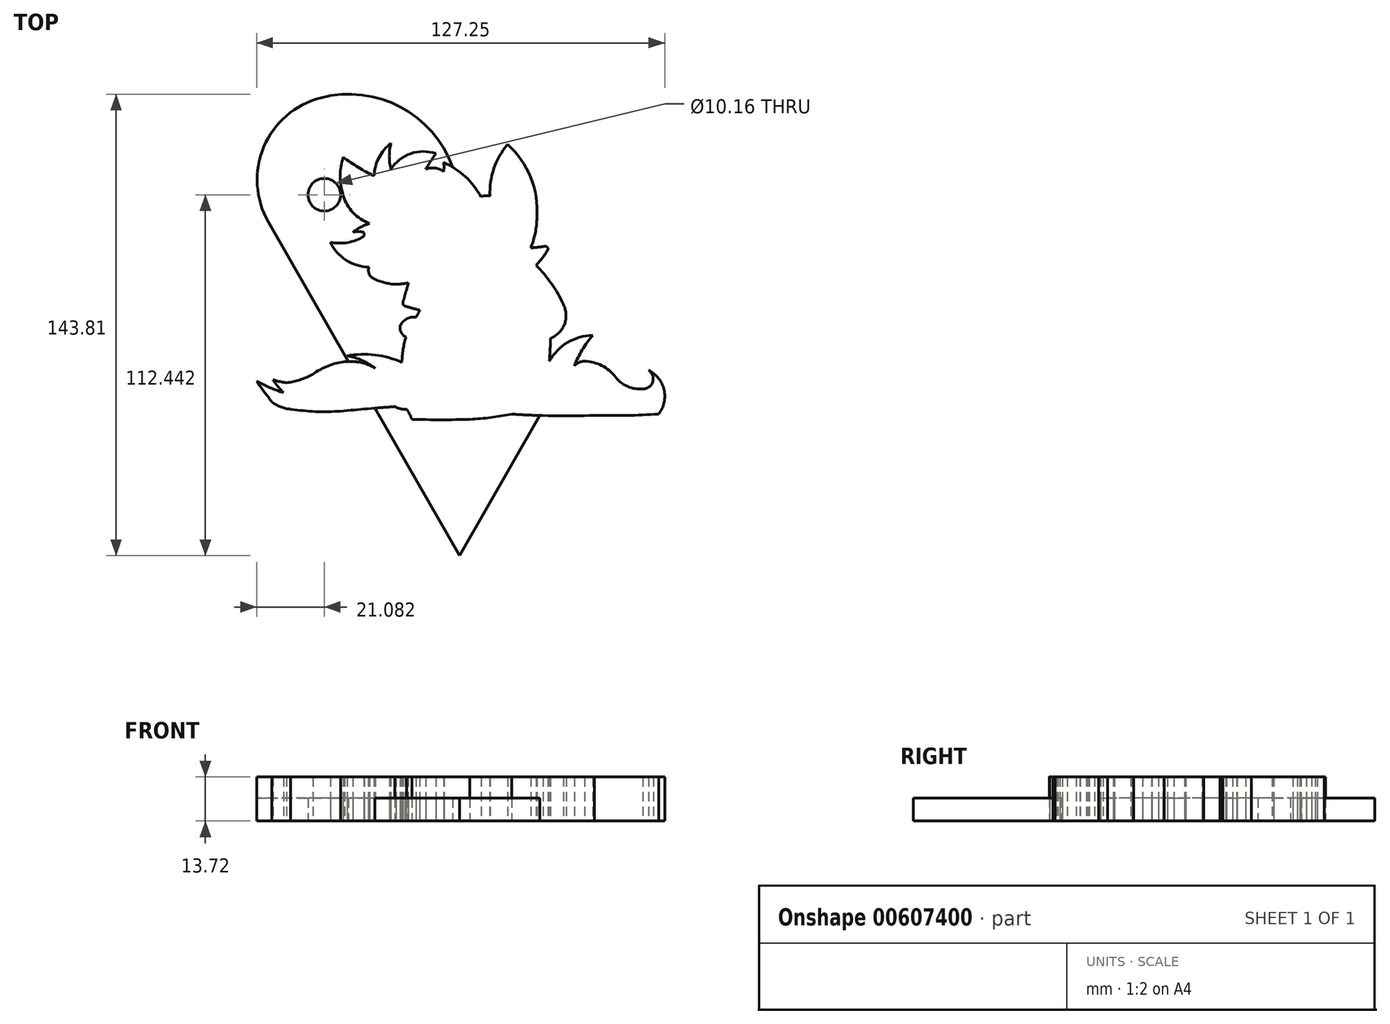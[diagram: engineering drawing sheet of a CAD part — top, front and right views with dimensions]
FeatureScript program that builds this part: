
annotation { "Feature Type Name" : "Feature", "Feature Type Description" : "" }
export const myFeature = defineFeature(function(context is Context, id is Id, definition is map)
    precondition{}
    {
        {
            var Q0;
            Q0=qCreatedBy(makeId("Top.planeOp"),FACE);
            var sketch = newSketch(context, id + "F0", { "sketchPlane" : qUnion([Q0])});
            skArc(sketch, "E0", {"start": v(-40.37, 7.34) * mm, "mid": v(-35.43, 1.75) * mm, "end": v(-28.28, -0.4) * mm});
            skArc(sketch, "E1", {"start": v(-28.28, -0.4) * mm, "mid": v(-28.3, -2.46) * mm, "end": v(-26.9, -3.99) * mm});
            skArc(sketch, "E2", {"start": v(-26.9, -3.99) * mm, "mid": v(-23.5, -5.25) * mm, "end": v(-19.91, -5.8) * mm});
            skArc(sketch, "E3", {"start": v(-19.91, -5.8) * mm, "mid": v(-17.97, -5.63) * mm, "end": v(-16.04, -5.38) * mm});
            skArc(sketch, "E4", {"start": v(-17.13, -9.12) * mm, "mid": v(-16.52, -7.27) * mm, "end": v(-16.04, -5.38) * mm});
            skArc(sketch, "E5", {"start": v(-17.65, -11.1) * mm, "mid": v(-17.34, -10.13) * mm, "end": v(-17.13, -9.12) * mm});
            skArc(sketch, "E6", {"start": v(-17.65, -11.1) * mm, "mid": v(-17.7, -11.94) * mm, "end": v(-17.13, -12.56) * mm});
            skArc(sketch, "E7", {"start": v(-17.13, -12.56) * mm, "mid": v(-14.8, -13.21) * mm, "end": v(-12.46, -13.87) * mm});
            skArc(sketch, "E8", {"start": v(-12.46, -13.87) * mm, "mid": v(-13.05, -14.97) * mm, "end": v(-13.6, -16.08) * mm});
            skArc(sketch, "E9", {"start": v(-13.6, -16.08) * mm, "mid": v(-16.6, -16.57) * mm, "end": v(-18.61, -18.86) * mm});
            skArc(sketch, "E10", {"start": v(-18.61, -18.86) * mm, "mid": v(-18.28, -20.87) * mm, "end": v(-16.75, -22.22) * mm});
            skArc(sketch, "E11", {"start": v(-16.75, -22.22) * mm, "mid": v(-17.7, -26.1) * mm, "end": v(-18.04, -30.06) * mm});
            skArc(sketch, "E12", {"start": v(-18.04, -30.06) * mm, "mid": v(-26.4, -27.8) * mm, "end": v(-35.06, -28.06) * mm});
            skArc(sketch, "E13", {"start": v(-26.36, -31.93) * mm, "mid": v(-30.48, -29.47) * mm, "end": v(-35.06, -28.06) * mm});
            skArc(sketch, "E14", {"start": v(-26.36, -31.93) * mm, "mid": v(-30.95, -30.12) * mm, "end": v(-35.86, -29.92) * mm});
            skArc(sketch, "E15", {"start": v(-35.86, -29.92) * mm, "mid": v(-41.1, -31.2) * mm, "end": v(-45.82, -33.82) * mm});
            skArc(sketch, "E16", {"start": v(-54.02, -36.45) * mm, "mid": v(-49.8, -35.53) * mm, "end": v(-45.82, -33.82) * mm});
            skArc(sketch, "E17", {"start": v(-58.23, -35.53) * mm, "mid": v(-56.14, -36.1) * mm, "end": v(-54.02, -36.45) * mm});
            skArc(sketch, "E18", {"start": v(-58.23, -35.53) * mm, "mid": v(-56.69, -37.64) * mm, "end": v(-54.93, -39.57) * mm});
            skArc(sketch, "E19", {"start": v(-63.33, -35.96) * mm, "mid": v(-59.21, -37.96) * mm, "end": v(-54.93, -39.57) * mm});
            skArc(sketch, "E20", {"start": v(-63.33, -35.96) * mm, "mid": v(-61.02, -39.24) * mm, "end": v(-58.55, -42.4) * mm});
            skArc(sketch, "E21", {"start": v(-58.55, -42.4) * mm, "mid": v(-55.81, -44.01) * mm, "end": v(-52.7, -44.68) * mm});
            skArc(sketch, "E22", {"start": v(-52.7, -44.68) * mm, "mid": v(-44.95, -45.44) * mm, "end": v(-37.16, -45.3) * mm});
            skArc(sketch, "E23", {"start": v(-20.24, -43.88) * mm, "mid": v(-28.7, -44.56) * mm, "end": v(-37.16, -45.3) * mm});
            skArc(sketch, "E24", {"start": v(-20.24, -43.88) * mm, "mid": v(-18.46, -44.58) * mm, "end": v(-16.55, -44.68) * mm});
            skArc(sketch, "E25", {"start": v(-14.9, -47.86) * mm, "mid": v(-15.65, -46.23) * mm, "end": v(-16.55, -44.68) * mm});
            skArc(sketch, "E26", {"start": v(-14.9, -47.86) * mm, "mid": v(-5.87, -48) * mm, "end": v(3.17, -47.86) * mm});
            skArc(sketch, "E27", {"start": v(3.17, -47.86) * mm, "mid": v(9.74, -47.27) * mm, "end": v(16.25, -46.21) * mm});
            skArc(sketch, "E28", {"start": v(16.25, -46.21) * mm, "mid": v(29.1, -46.76) * mm, "end": v(41.96, -46.59) * mm});
            skArc(sketch, "E29", {"start": v(41.96, -46.59) * mm, "mid": v(52, -46.65) * mm, "end": v(62.02, -46.21) * mm});
            skArc(sketch, "E30", {"start": v(62.02, -46.21) * mm, "mid": v(63.69, -38.64) * mm, "end": v(58.88, -32.56) * mm});
            skArc(sketch, "E31", {"start": v(57.1, -38.36) * mm, "mid": v(60.2, -36.14) * mm, "end": v(58.88, -32.56) * mm});
            skArc(sketch, "E32", {"start": v(48.61, -34.71) * mm, "mid": v(52.37, -37.65) * mm, "end": v(57.1, -38.36) * mm});
            skArc(sketch, "E33", {"start": v(48.61, -34.71) * mm, "mid": v(44.3, -31.11) * mm, "end": v(38.87, -29.74) * mm});
            skArc(sketch, "E34", {"start": v(38.87, -29.74) * mm, "mid": v(37.14, -30.14) * mm, "end": v(35.72, -31.21) * mm});
            skArc(sketch, "E35", {"start": v(41.46, -21.68) * mm, "mid": v(38.2, -26.21) * mm, "end": v(35.72, -31.21) * mm});
            skArc(sketch, "E36", {"start": v(41.46, -21.68) * mm, "mid": v(33.63, -23.91) * mm, "end": v(27.94, -29.74) * mm});
            skArc(sketch, "E37", {"start": v(27.94, -29.74) * mm, "mid": v(28.17, -26.17) * mm, "end": v(28.29, -22.6) * mm});
            skArc(sketch, "E38", {"start": v(28.29, -22.6) * mm, "mid": v(32.65, -18.26) * mm, "end": v(32.34, -12.11) * mm});
            skArc(sketch, "E39", {"start": v(32.34, -12.11) * mm, "mid": v(28.62, -5.58) * mm, "end": v(23.77, 0.16) * mm});
            skArc(sketch, "E40", {"start": v(23.77, 0.16) * mm, "mid": v(25.84, 2.55) * mm, "end": v(27.56, 5.2) * mm});
            skArc(sketch, "E41", {"start": v(27.56, 5.2) * mm, "mid": v(26.99, 6) * mm, "end": v(26, 5.94) * mm});
            skArc(sketch, "E42", {"start": v(26, 5.94) * mm, "mid": v(24.06, 5.75) * mm, "end": v(22.12, 5.53) * mm});
            skArc(sketch, "E43", {"start": v(22.12, 5.53) * mm, "mid": v(23.52, 10.17) * mm, "end": v(24.03, 14.99) * mm});
            skArc(sketch, "E44", {"start": v(24.03, 14.99) * mm, "mid": v(22.16, 27.47) * mm, "end": v(14.92, 37.8) * mm});
            skArc(sketch, "E45", {"start": v(9.41, 21.73) * mm, "mid": v(7.98, 21.87) * mm, "end": v(6.6, 21.45) * mm});
            skArc(sketch, "E46", {"start": v(14.92, 37.8) * mm, "mid": v(10.64, 30.29) * mm, "end": v(9.41, 21.73) * mm});
            skArc(sketch, "E47", {"start": v(6.6, 21.45) * mm, "mid": v(1.7, 27.8) * mm, "end": v(-5.02, 32.18) * mm});
            skArc(sketch, "E48", {"start": v(-5.02, 29.37) * mm, "mid": v(-4.92, 30.77) * mm, "end": v(-5.02, 32.18) * mm});
            skArc(sketch, "E49", {"start": v(-5.02, 29.37) * mm, "mid": v(-7.72, 30.46) * mm, "end": v(-10.6, 30.08) * mm});
            skArc(sketch, "E50", {"start": v(-7.42, 34.97) * mm, "mid": v(-9.08, 32.57) * mm, "end": v(-10.6, 30.08) * mm});
            skArc(sketch, "E51", {"start": v(-7.42, 34.97) * mm, "mid": v(-15.29, 34.96) * mm, "end": v(-21.46, 30.08) * mm});
            skArc(sketch, "E52", {"start": v(-21.46, 38.17) * mm, "mid": v(-21.97, 34.12) * mm, "end": v(-21.46, 30.08) * mm});
            skArc(sketch, "E53", {"start": v(-21.46, 38.17) * mm, "mid": v(-25.21, 33.69) * mm, "end": v(-26.7, 28.04) * mm});
            skArc(sketch, "E54", {"start": v(-36.33, 33.86) * mm, "mid": v(-31.67, 30.69) * mm, "end": v(-26.7, 28.04) * mm});
            skArc(sketch, "E55", {"start": v(-40.37, 7.34) * mm, "mid": v(-34.96, 7.25) * mm, "end": v(-29.9, 9.18) * mm});
            skArc(sketch, "E56", {"start": v(-29.9, 9.18) * mm, "mid": v(-29.82, 9.8) * mm, "end": v(-29.9, 10.43) * mm});
            skArc(sketch, "E57", {"start": v(-29.9, 10.43) * mm, "mid": v(-31.64, 10.64) * mm, "end": v(-33.37, 10.43) * mm});
            skArc(sketch, "E58", {"start": v(-28.1, 13.2) * mm, "mid": v(-30.86, 12.05) * mm, "end": v(-33.37, 10.43) * mm});
            skArc(sketch, "E59", {"start": v(-36.33, 21.97) * mm, "mid": v(-33.3, 16.58) * mm, "end": v(-28.1, 13.2) * mm});
            skArc(sketch, "E60", {"start": v(-36.33, 33.86) * mm, "mid": v(-37.3, 27.91) * mm, "end": v(-36.33, 21.97) * mm});
            skSolve(sketch);
        }
        {
            var Q0;
            Q0=makeQuery(id+"F0.imprint","IMPRINT",FACE,{"disambiguationData":[TD([[makeQuery(id+"F0.imprint","IMPRINT",EDGE,{"derivedFrom":sQuery(id+"F0.wireOp",EDGE,"E0")}),1.0]])]});
            var sketch = newSketch(context, id + "F1", { "sketchPlane" : qUnion([Q0])});
            skLineSegment(sketch, "E61", {"start": v(-59.66, 13.61) * mm, "end": v(-0.11, -90.32) * mm});
            skArc(sketch, "E62", {"start": v(-43.38, 52.36) * mm, "mid": v(-61.1, 37) * mm, "end": v(-59.66, 13.61) * mm});
            skArc(sketch, "E63", {"start": v(-0.11, 18.97) * mm, "mid": v(-13.54, 46.3) * mm, "end": v(-43.38, 52.36) * mm});
            skArc(sketch, "E64.MirrorCS", {"start": v(-0.11, 18.97) * mm, "mid": v(13.32, 46.3) * mm, "end": v(43.16, 52.36) * mm});
            skLineSegment(sketch, "E65.MirrorCS", {"start": v(59.44, 13.61) * mm, "end": v(-0.11, -90.32) * mm});
            skArc(sketch, "E66.MirrorCS", {"start": v(43.16, 52.36) * mm, "mid": v(60.88, 37) * mm, "end": v(59.44, 13.61) * mm});
            skSolve(sketch);
        }
        {
            var Q0;
            {var subQ5=sQuery(id+"F1.wireOp",EDGE,"E62");Q0=makeQuery(id+"F1.imprint","IMPRINT",FACE,{"disambiguationData":[TD([[makeQuery(id+"F1.imprint","IMPRINT",EDGE,{"derivedFrom":subQ5}),1.0]])]});}
            var Q1;
            {var subQ0=sQuery(id+"F1.wireOp",EDGE,"E66.MirrorCS");Q1=makeQuery(id+"F1.imprint","IMPRINT",FACE,{"disambiguationData":[TD([[makeQuery(id+"F1.imprint","IMPRINT",EDGE,{"derivedFrom":subQ0}),-1.0]])]});}
            var Q2;
            {var subQ0=makeQuery(id+"F0.imprint","IMPRINT",EDGE,{"derivedFrom":sQuery(id+"F0.wireOp",EDGE,"E24")});Q2=makeQuery(id+"F1.imprint","IMPRINT",FACE,{"disambiguationData":[TD([[makeQuery(id+"F1.imprint","IMPRINT",EDGE,{"derivedFrom":subQ0}),-1.0]])]});}
            extrude(context, id + "F2", {"entities" : qUnion([Q0, Q1, Q2]), "depth" : 7.11 * mm, "offsetDistance" : 25.4 * mm});
        }
        {
            var Q0;
            Q0=makeQuery(id+"F0.imprint","IMPRINT",FACE,{"disambiguationData":[TD([[makeQuery(id+"F0.imprint","IMPRINT",EDGE,{"derivedFrom":sQuery(id+"F0.wireOp",EDGE,"E0")}),1.0]])]});
            extrude(context, id + "F3", {"entities" : qUnion([Q0]), "depth" : 13.72 * mm, "offsetDistance" : 25.4 * mm});
        }
        {
            var Q0;
            Q0=sQuery(id+"F0.wireOp",VERTEX,"E22.center");
            var Q1;
            Q1=makeQuery(id+"F2.opExtrude","SWEPT_BODY",BODY,{"disambiguationData":[OSD([sQuery(id+"F0.wireOp",EDGE,"E0"),sQuery(id+"F0.wireOp",EDGE,"E1"),sQuery(id+"F0.wireOp",EDGE,"E2"),sQuery(id+"F0.wireOp",EDGE,"E3"),sQuery(id+"F0.wireOp",EDGE,"E4"),sQuery(id+"F0.wireOp",EDGE,"E5"),sQuery(id+"F0.wireOp",EDGE,"E6"),sQuery(id+"F0.wireOp",EDGE,"E7"),sQuery(id+"F0.wireOp",EDGE,"E8"),sQuery(id+"F0.wireOp",EDGE,"E9"),sQuery(id+"F0.wireOp",EDGE,"E10"),sQuery(id+"F0.wireOp",EDGE,"E11"),sQuery(id+"F0.wireOp",EDGE,"E12"),sQuery(id+"F0.wireOp",EDGE,"E13"),sQuery(id+"F0.wireOp",EDGE,"E14"),sQuery(id+"F0.wireOp",EDGE,"E47"),sQuery(id+"F0.wireOp",EDGE,"E48"),sQuery(id+"F0.wireOp",EDGE,"E49"),sQuery(id+"F0.wireOp",EDGE,"E50"),sQuery(id+"F0.wireOp",EDGE,"E51"),sQuery(id+"F0.wireOp",EDGE,"E52"),sQuery(id+"F0.wireOp",EDGE,"E53"),sQuery(id+"F0.wireOp",EDGE,"E54"),sQuery(id+"F0.wireOp",EDGE,"E55"),sQuery(id+"F0.wireOp",EDGE,"E56"),sQuery(id+"F0.wireOp",EDGE,"E57"),sQuery(id+"F0.wireOp",EDGE,"E58"),sQuery(id+"F0.wireOp",EDGE,"E59"),sQuery(id+"F0.wireOp",EDGE,"E60"),sQuery(id+"F1.wireOp",EDGE,"E61"),sQuery(id+"F1.wireOp",EDGE,"E62"),sQuery(id+"F1.wireOp",EDGE,"E63")])]});
            hole(context, id + "F4", {"style" : HoleStyle.SIMPLE, "endStyle" : HoleEndStyle.THROUGH, "oppositeDirection" : true, "holeDiameter" : 10.16 * mm, "majorDiameter" : 6.35 * mm, "isTappedThrough" : true, "tappedDepth" : 12.7 * mm, "tapClearance" : 3, "locations" : qUnion([Q0]), "scope" : qUnion([Q1])});
        }
    });
